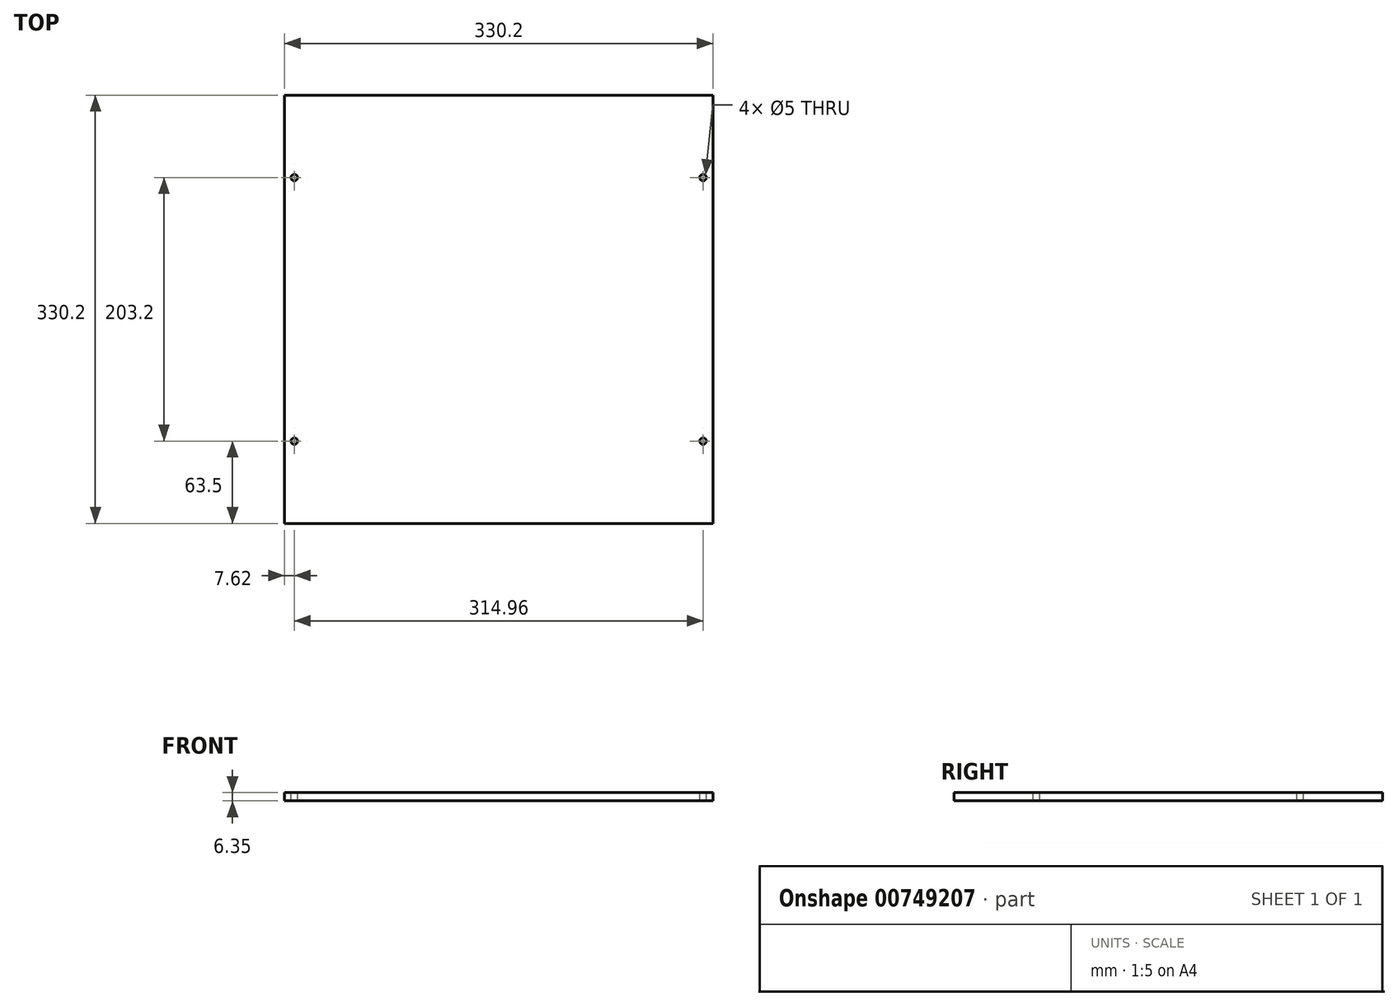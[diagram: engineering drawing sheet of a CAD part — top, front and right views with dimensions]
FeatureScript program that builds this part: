
annotation { "Feature Type Name" : "Feature", "Feature Type Description" : "" }
export const myFeature = defineFeature(function(context is Context, id is Id, definition is map)
    precondition{}
    {
        {
            var Q0;
            Q0=qCreatedBy(makeId("Top.planeOp"),FACE);
            var sketch = newSketch(context, id + "F0", { "sketchPlane" : qUnion([Q0])});
            skLineSegment(sketch, "E0.bottom", {"start": v(0, 0) * mm, "end": v(330.2, 0) * mm});
            skLineSegment(sketch, "E0.top", {"start": v(0, 330.2) * mm, "end": v(330.2, 330.2) * mm});
            skLineSegment(sketch, "E0.left", {"start": v(0, 0) * mm, "end": v(0, 330.2) * mm});
            skLineSegment(sketch, "E0.right", {"start": v(330.2, 0) * mm, "end": v(330.2, 330.2) * mm});
            skSolve(sketch);
        }
        {
            var Q0;
            Q0=qSketchRegion(id+"F0",true);
            extrude(context, id + "F1", {"entities" : qUnion([Q0]), "depth" : 6.35 * mm, "offsetDistance" : 25.4 * mm});
        }
        {
            var Q0;
            Q0=makeQuery(id+"F1.opExtrude","CAP_FACE",FACE,{"disambiguationData":[OSD([sQuery(id+"F0.wireOp",EDGE,"E0.bottom"),sQuery(id+"F0.wireOp",EDGE,"E0.top"),sQuery(id+"F0.wireOp",EDGE,"E0.left"),sQuery(id+"F0.wireOp",EDGE,"E0.right")])],"isStart":false});
            var sketch = newSketch(context, id + "F2", { "sketchPlane" : qUnion([Q0])});
            skCircle(sketch, "E1", {"center": v(7.62, 266.7) * mm, "radius": 2.5 * mm});
            skCircle(sketch, "E2", {"center": v(322.58, 266.7) * mm, "radius": 2.5 * mm});
            skCircle(sketch, "E3", {"center": v(322.58, 63.5) * mm, "radius": 2.5 * mm});
            skCircle(sketch, "E4", {"center": v(7.62, 63.5) * mm, "radius": 2.5 * mm});
            skSolve(sketch);
        }
        {
            var Q0;
            Q0=qSketchRegion(id+"F2",true);
            extrude(context, id + "F3", {"entities" : qUnion([Q0]), "operationType" : NewBodyOperationType.REMOVE, "oppositeDirection" : true, "depth" : 25.4 * mm, "offsetDistance" : 25.4 * mm});
        }
    });
